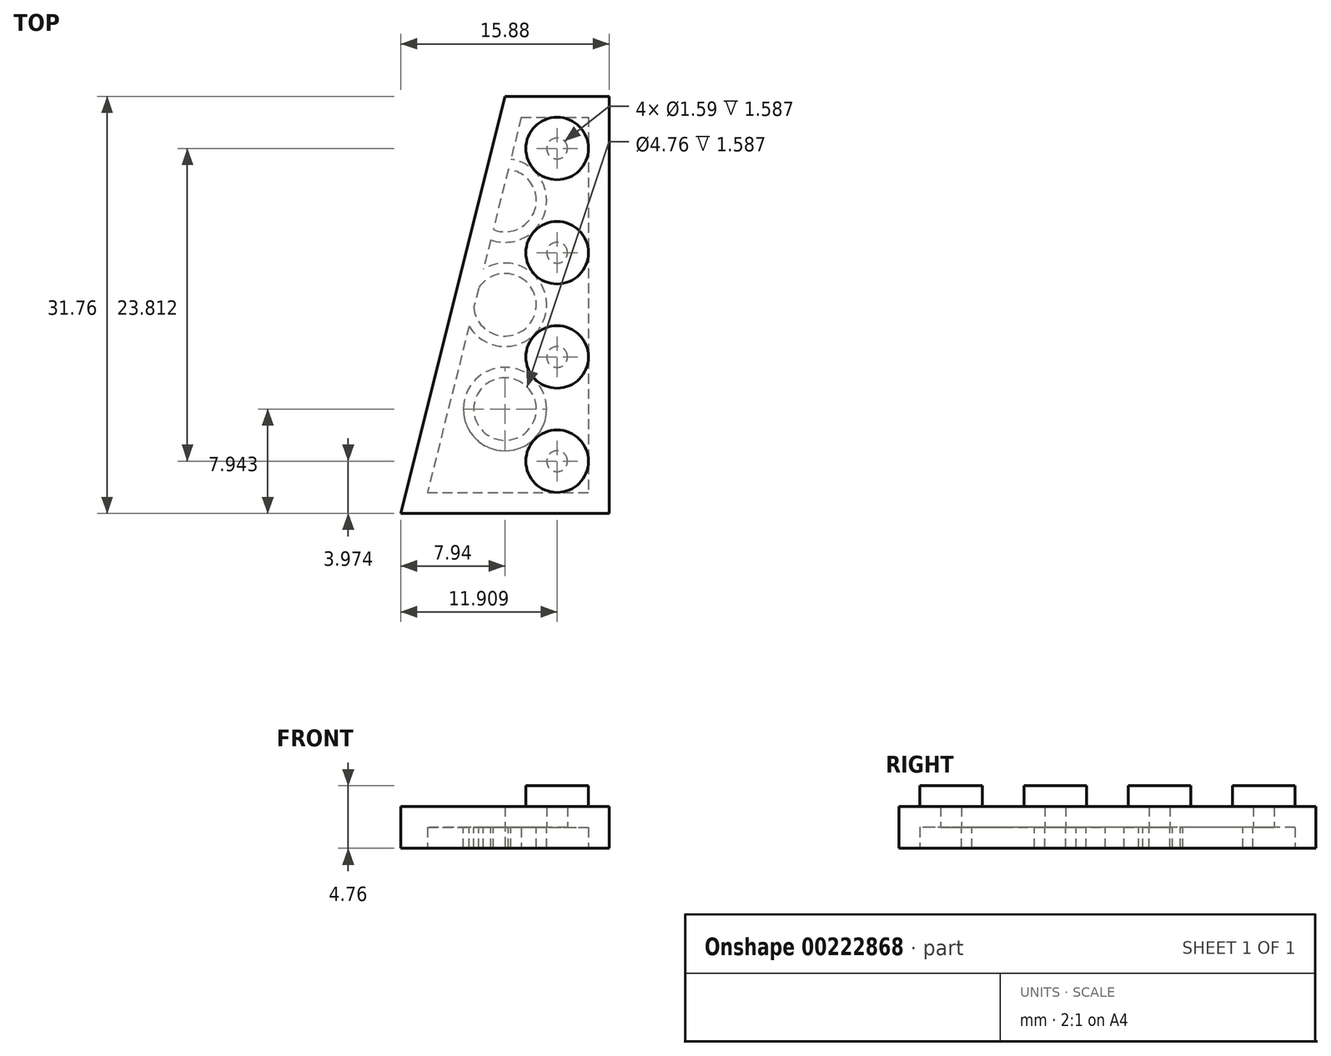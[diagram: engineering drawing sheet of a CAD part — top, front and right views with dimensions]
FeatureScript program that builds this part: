
annotation { "Feature Type Name" : "Feature", "Feature Type Description" : "" }
export const myFeature = defineFeature(function(context is Context, id is Id, definition is map)
    precondition{}
    {
        {
            var Q0;
            Q0=qCreatedBy(makeId("Top.planeOp"),FACE);
            var sketch = newSketch(context, id + "F0", { "sketchPlane" : qUnion([Q0])});
            skLineSegment(sketch, "E0.bottom", {"start": v(-7.94, 15.88) * mm, "end": v(7.94, 15.88) * mm});
            skLineSegment(sketch, "E0.top", {"start": v(-7.94, -15.88) * mm, "end": v(7.94, -15.88) * mm});
            skLineSegment(sketch, "E0.left", {"start": v(-7.94, 15.88) * mm, "end": v(-7.94, -15.88) * mm});
            skLineSegment(sketch, "E0.right", {"start": v(7.94, 15.88) * mm, "end": v(7.94, -15.88) * mm});
            skPoint(sketch, "E0.middle", {"position": v(0, 0) * mm});
            skCircle(sketch, "E1", {"center": v(3.97, -11.9) * mm, "radius": 2.38 * mm});
            skCircle(sketch, "E2.0.1.0", {"center": v(3.97, -3.97) * mm, "radius": 2.38 * mm});
            skLineSegment(sketch, "E2.direction1", {"start": v(3.97, -11.9) * mm, "end": v(29.37, -11.9) * mm, "construction": true});
            skLineSegment(sketch, "E2.direction2", {"start": v(3.97, -11.9) * mm, "end": v(3.97, -3.97) * mm, "construction": true});
            skCircle(sketch, "E3.0.0.2", {"center": v(3.97, 3.97) * mm, "radius": 2.38 * mm});
            skCircle(sketch, "E3.0.0.3", {"center": v(3.97, 11.9) * mm, "radius": 2.38 * mm});
            skPoint(sketch, "E4", {"position": v(0, 15.88) * mm});
            skLineSegment(sketch, "E5", {"start": v(0, 15.88) * mm, "end": v(-7.94, -15.88) * mm});
            skSolve(sketch);
        }
        {
            var Q0;
            {var subQ0=sQuery(id+"F0.wireOp",EDGE,"E0.right");Q0=makeQuery(id+"F0.imprint","IMPRINT",FACE,{"disambiguationData":[TD([[makeQuery(id+"F0.imprint","IMPRINT",EDGE,{"derivedFrom":subQ0}),-1.0]])]});}
            extrude(context, id + "F1", {"entities" : qUnion([Q0]), "depth" : 3.17 * mm});
        }
        {
            var Q0;
            Q0=makeQuery(id+"F0.imprint","IMPRINT",FACE,{"disambiguationData":[TD([[makeQuery(id+"F0.imprint","IMPRINT",EDGE,{"derivedFrom":sQuery(id+"F0.wireOp",EDGE,"E3.0.0.3")}),1.0]])]});
            var Q1;
            Q1=makeQuery(id+"F0.imprint","IMPRINT",FACE,{"disambiguationData":[TD([[makeQuery(id+"F0.imprint","IMPRINT",EDGE,{"derivedFrom":sQuery(id+"F0.wireOp",EDGE,"E3.0.0.2")}),1.0]])]});
            var Q2;
            Q2=makeQuery(id+"F0.imprint","IMPRINT",FACE,{"disambiguationData":[TD([[makeQuery(id+"F0.imprint","IMPRINT",EDGE,{"derivedFrom":sQuery(id+"F0.wireOp",EDGE,"E2.0.1.0")}),1.0]])]});
            var Q3;
            Q3=makeQuery(id+"F0.imprint","IMPRINT",FACE,{"disambiguationData":[TD([[makeQuery(id+"F0.imprint","IMPRINT",EDGE,{"derivedFrom":sQuery(id+"F0.wireOp",EDGE,"E1")}),1.0]])]});
            extrude(context, id + "F2", {"entities" : qUnion([Q0, Q1, Q2, Q3]), "operationType" : NewBodyOperationType.ADD, "depth" : 4.76 * mm});
        }
        {
            var Q0;
            {var subQ0=sQuery(id+"F0.wireOp",EDGE,"E3.0.0.3");var subQ1=sQuery(id+"F0.wireOp",EDGE,"E3.0.0.2");var subQ2=sQuery(id+"F0.wireOp",EDGE,"E2.0.1.0");var subQ3=sQuery(id+"F0.wireOp",EDGE,"E1");Q0=makeQuery(id+"F2.boolean.opBoolean","MERGE",FACE,{"derivedFrom":[makeQuery(id+"F1.opExtrude","CAP_FACE",FACE,{"disambiguationData":[OSD([sQuery(id+"F0.wireOp",EDGE,"E0.bottom"),sQuery(id+"F0.wireOp",EDGE,"E0.top"),sQuery(id+"F0.wireOp",EDGE,"E0.left"),sQuery(id+"F0.wireOp",EDGE,"E0.right"),subQ3,subQ2,subQ1,subQ0])],"isStart":true}),makeQuery(id+"F2.opExtrude","CAP_FACE",FACE,{"disambiguationData":[OSD([subQ3])],"isStart":true}),makeQuery(id+"F2.opExtrude","CAP_FACE",FACE,{"disambiguationData":[OSD([subQ2])],"isStart":true}),makeQuery(id+"F2.opExtrude","CAP_FACE",FACE,{"disambiguationData":[OSD([subQ1])],"isStart":true}),makeQuery(id+"F2.opExtrude","CAP_FACE",FACE,{"disambiguationData":[OSD([subQ0])],"isStart":true})]});}
            shell(context, id + "F3", {"entities" : qUnion([Q0]), "thickness" : 1.59 * mm});
        }
        {
            var Q0;
            Q0=makeQuery(id+"F3.opShell","OFFSET_FACE",FACE,{"disambiguationData":[OSD([sQuery(id+"F0.wireOp",EDGE,"E0.bottom"),sQuery(id+"F0.wireOp",EDGE,"E0.top"),sQuery(id+"F0.wireOp",EDGE,"E0.left"),sQuery(id+"F0.wireOp",EDGE,"E0.right"),sQuery(id+"F0.wireOp",EDGE,"E1"),sQuery(id+"F0.wireOp",EDGE,"E2.0.1.0"),sQuery(id+"F0.wireOp",EDGE,"E3.0.0.2"),sQuery(id+"F0.wireOp",EDGE,"E3.0.0.3")])]});
            var sketch = newSketch(context, id + "F4", { "sketchPlane" : qUnion([Q0])});
            skCircle(sketch, "E6", {"center": v(0, -7.94) * mm, "radius": 3.18 * mm});
            skCircle(sketch, "E7", {"center": v(0, -7.94) * mm, "radius": 2.38 * mm});
            skCircle(sketch, "E8.0.1.0", {"center": v(0, 0) * mm, "radius": 3.18 * mm});
            skCircle(sketch, "E8.0.1.1", {"center": v(0, 0) * mm, "radius": 2.38 * mm});
            skCircle(sketch, "E8.0.2.0", {"center": v(0, 7.94) * mm, "radius": 3.18 * mm});
            skCircle(sketch, "E8.0.2.1", {"center": v(0, 7.94) * mm, "radius": 2.38 * mm});
            skLineSegment(sketch, "E8.direction1", {"start": v(0, -7.94) * mm, "end": v(25.4, -7.94) * mm, "construction": true});
            skLineSegment(sketch, "E8.direction2", {"start": v(0, -7.94) * mm, "end": v(0, 0) * mm, "construction": true});
            skSolve(sketch);
        }
        {
            var Q0;
            Q0=makeQuery(id+"F4.imprint","IMPRINT",FACE,{"disambiguationData":[TD([[makeQuery(id+"F4.imprint","IMPRINT",EDGE,{"derivedFrom":sQuery(id+"F4.wireOp",EDGE,"E8.0.2.0")}),1.0]])]});
            var Q1;
            {var subQ0=sQuery(id+"F4.wireOp",EDGE,"E8.0.1.0");var subQ1=sQuery(id+"F0.wireOp",EDGE,"E5");var subQ2=makeQuery(id+"F3.opShell","OFFSET_EDGE",EDGE,{"disambiguationData":[OSD([subQ1]),TDD([makeQuery(id+"F1.opExtrude","CAP_EDGE",EDGE,{"disambiguationData":[OSD([subQ1])],"isStart":false})])]});var subQ3=makeQuery(id+"F4.imprint","INTERSECT",VERTEX,{"disambiguationData":[OD(0.0)],"derivedFrom":[subQ2,subQ0]});Q1=makeQuery(id+"F4.imprint","IMPRINT",FACE,{"disambiguationData":[TD([[makeQuery(id+"F4.imprint","IMPRINT",EDGE,{"disambiguationData":[TD([[subQ3,1.0]])],"derivedFrom":subQ0}),1.0]])]});}
            var Q2;
            {var subQ0=sQuery(id+"F4.wireOp",EDGE,"E6");var subQ1=sQuery(id+"F0.wireOp",EDGE,"E5");var subQ2=makeQuery(id+"F3.opShell","OFFSET_EDGE",EDGE,{"disambiguationData":[OSD([subQ1]),TDD([makeQuery(id+"F1.opExtrude","CAP_EDGE",EDGE,{"disambiguationData":[OSD([subQ1])],"isStart":false})])]});var subQ3=makeQuery(id+"F4.imprint","INTERSECT",VERTEX,{"disambiguationData":[OD(0.0)],"derivedFrom":[subQ2,subQ0]});Q2=makeQuery(id+"F4.imprint","IMPRINT",FACE,{"disambiguationData":[TD([[makeQuery(id+"F4.imprint","IMPRINT",EDGE,{"disambiguationData":[TD([[subQ3,-1.0]])],"derivedFrom":subQ0}),1.0]])]});}
            extrude(context, id + "F5", {"entities" : qUnion([Q0, Q1, Q2]), "operationType" : NewBodyOperationType.ADD, "depth" : 1.59 * mm});
        }
    });
